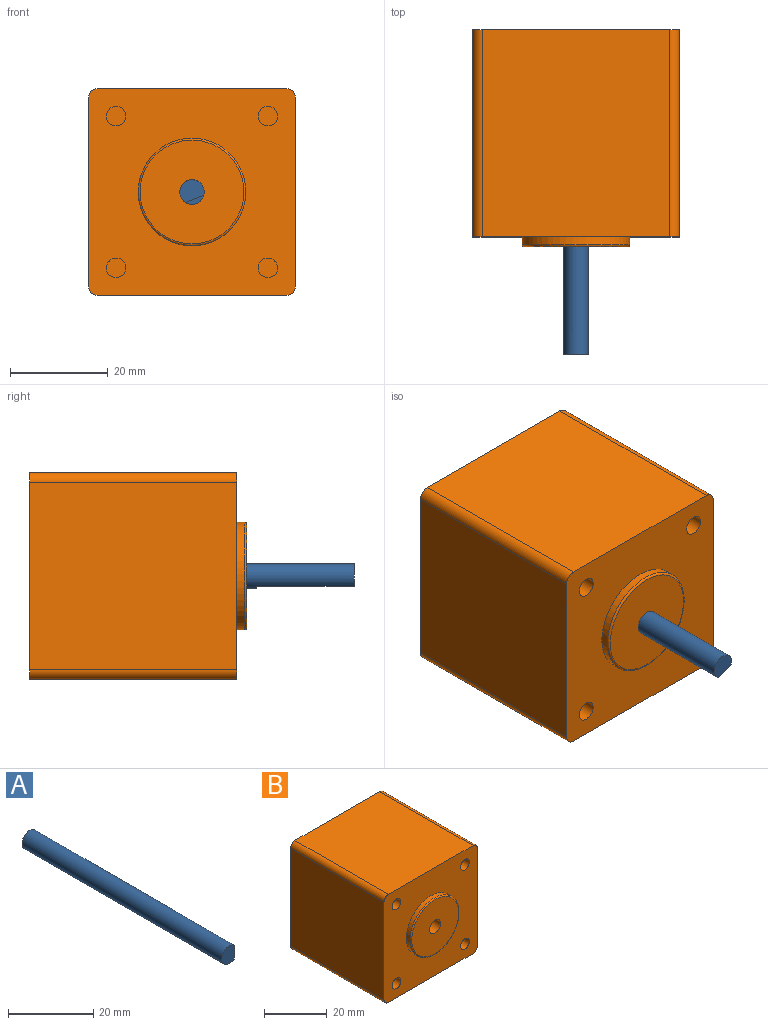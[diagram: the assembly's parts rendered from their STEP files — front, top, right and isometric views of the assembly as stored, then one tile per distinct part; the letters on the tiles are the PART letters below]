
ASSEMBLY  parts=2 mates=1
PART A: 5 faces, bbox 5x66.3x5 mm
  f0: plane 5x4mm, normal (0,-1,0), area 16.8mm2, adj f2,f3
  f1: plane 5x5mm, normal (0,1,0), area 19.6mm2, adj f2
  f2: cylinder r=2.5mm len=66.3mm, axis (0,1,0), area 948.7mm2, adj f0,f1,f3,f4
  f3: plane 20x4mm, normal (1,0,0), area 80mm2, adj f0,f2,f4
  f4: plane 4x1mm, normal (0,-1,0), area 2.8mm2, adj f2,f3
PART B: 22 faces, bbox 42.3x44.3x42.3 mm
  f0: plane 42.3x38.3mm, normal (0,0,-1), area 1620.1mm2, adj f5,f6,f18,f21
  f1: plane 42.3x38.3mm, normal (1,0,0), area 1620.1mm2, adj f5,f6,f18,f19
  f2: plane 42.3x38.3mm, normal (0,0,1), area 1620.1mm2, adj f5,f6,f19,f20
  f3: cylinder r=2.5mm len=44.3mm, axis (0,-1,0), area 695.9mm2, adj f5,f8
  f4: plane 42.3x38.3mm, normal (-1,0,0), area 1620.1mm2, adj f5,f6,f20,f21
  f5: plane 42.3x42.3mm, normal (0,1,0), area 1766.2mm2, adj f0,f1,f2,f3,f4,f18,f19,f20
  f6: plane 42.3x42.3mm, normal (0,-1,0), area 1355.5mm2, adj f0,f1,f2,f4,f7,f9,f11,f13
  f7: cylinder r=11mm len=22mm, axis (0,1,0), area 110.6mm2, adj f6,f17
  f8: plane 21.2x21.2mm, normal (0,-1,0), area 333.4mm2, adj f3,f17
  f9: cylinder r=2mm len=10mm, axis (0,-1,0), area 125.7mm2, adj f6,f10
  f10: plane 4x4mm, normal (0,-1,0), area 12.6mm2, adj f9
  f11: cylinder r=2mm len=10mm, axis (0,-1,0), area 125.7mm2, adj f6,f12
  f12: plane 4x4mm, normal (0,-1,0), area 12.6mm2, adj f11
  f13: cylinder r=2mm len=10mm, axis (0,-1,0), area 125.7mm2, adj f6,f14
  f14: plane 4x4mm, normal (0,-1,0), area 12.6mm2, adj f13
  f15: cylinder r=2mm len=10mm, axis (0,-1,0), area 125.7mm2, adj f6,f16
  f16: plane 4x4mm, normal (0,-1,0), area 12.6mm2, adj f15
  f17: torus R=10.6mm, axis (0,-1,0), area 42.9mm2, adj f7,f8
  f18: cylinder r=2mm len=42.3mm, axis (0,1,0), area 132.9mm2, adj f0,f1,f5,f6
  f19: cylinder r=2mm len=42.3mm, axis (0,-1,0), area 132.9mm2, adj f1,f2,f5,f6
  f20: cylinder r=2mm len=42.3mm, axis (0,1,0), area 132.9mm2, adj f2,f4,f5,f6
  f21: cylinder r=2mm len=42.3mm, axis (0,-1,0), area 132.9mm2, adj f0,f4,f5,f6
PLACE A rot(axis=(0,1,0),68.4deg) t=(0.27,0.2,0.01)mm
PLACE B t=(0.27,0.2,0.01)mm fixed
MATE revolute B.f3 <-> A.f2  axis (0,-1,0) through (0.27,42.5,0.01)mm
